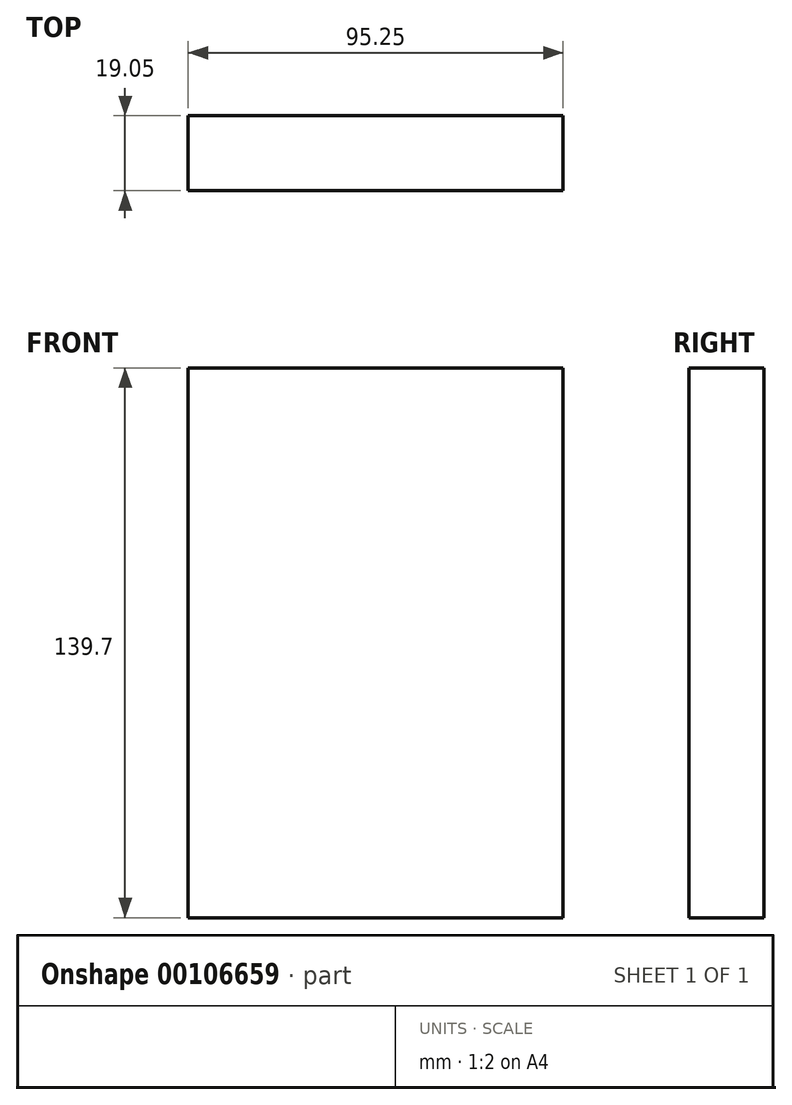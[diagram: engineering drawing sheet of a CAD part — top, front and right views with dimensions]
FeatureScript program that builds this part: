
annotation { "Feature Type Name" : "Feature", "Feature Type Description" : "" }
export const myFeature = defineFeature(function(context is Context, id is Id, definition is map)
    precondition{}
    {
        {
            var Q0;
            Q0=qCreatedBy(makeId("Front.planeOp"),FACE);
            var sketch = newSketch(context, id + "F0", { "sketchPlane" : qUnion([Q0])});
            skLineSegment(sketch, "E0.bottom", {"start": v(0, 0) * mm, "end": v(95.25, 0) * mm});
            skLineSegment(sketch, "E0.top", {"start": v(0, 139.7) * mm, "end": v(95.25, 139.7) * mm});
            skLineSegment(sketch, "E0.left", {"start": v(0, 0) * mm, "end": v(0, 139.7) * mm});
            skLineSegment(sketch, "E0.right", {"start": v(95.25, 0) * mm, "end": v(95.25, 139.7) * mm});
            skSolve(sketch);
        }
        {
            var Q0;
            Q0=makeQuery(id+"F0.imprint","IMPRINT",FACE,{"disambiguationData":[TD([[makeQuery(id+"F0.imprint","IMPRINT",EDGE,{"derivedFrom":sQuery(id+"F0.wireOp",EDGE,"E0.bottom")}),1.0]])]});
            extrude(context, id + "F1", {"entities" : qUnion([Q0]), "depth" : 19.05 * mm});
        }
    });
